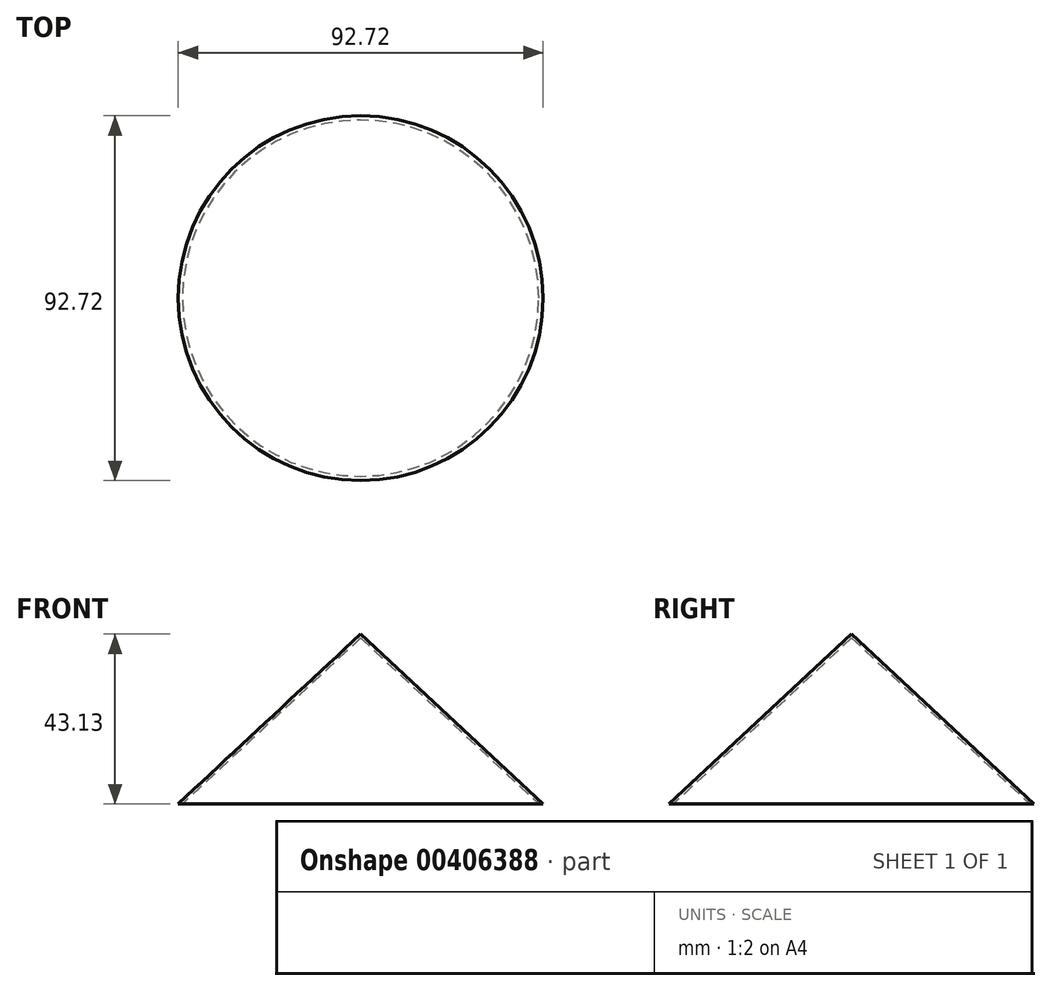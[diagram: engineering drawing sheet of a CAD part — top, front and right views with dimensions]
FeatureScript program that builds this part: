
annotation { "Feature Type Name" : "Feature", "Feature Type Description" : "" }
export const myFeature = defineFeature(function(context is Context, id is Id, definition is map)
    precondition{}
    {
        {
            var Q0;
            Q0=qCreatedBy(makeId("Front.planeOp"),FACE);
            var sketch = newSketch(context, id + "F0", { "sketchPlane" : qUnion([Q0])});
            skLineSegment(sketch, "E0", {"start": v(0, -84) * mm, "end": v(0, 93.4) * mm, "construction": true});
            skLineSegment(sketch, "E1", {"start": v(-46.36, 0) * mm, "end": v(0, 43.13) * mm});
            skLineSegment(sketch, "E2.0", {"start": v(-45.26, 0) * mm, "end": v(0, 42.1) * mm});
            skLineSegment(sketch, "E3", {"start": v(-46.36, 0) * mm, "end": v(-45.26, 0) * mm});
            skLineSegment(sketch, "E4", {"start": v(0, 43.13) * mm, "end": v(0, 42.1) * mm});
            skSolve(sketch);
        }
        {
            var Q0;
            Q0=makeQuery(id+"F0.imprint","IMPRINT",FACE,{"disambiguationData":[TD([[makeQuery(id+"F0.imprint","IMPRINT",EDGE,{"derivedFrom":sQuery(id+"F0.wireOp",EDGE,"E1")}),-1.0]])]});
            var Q1;
            Q1=sQuery(id+"F0.wireOp",EDGE,"E0");
            revolve(context, id + "F1", {"entities" : qUnion([Q0]), "axis" : qUnion([Q1]), "revolveType" : RevolveType.FULL});
        }
    });
